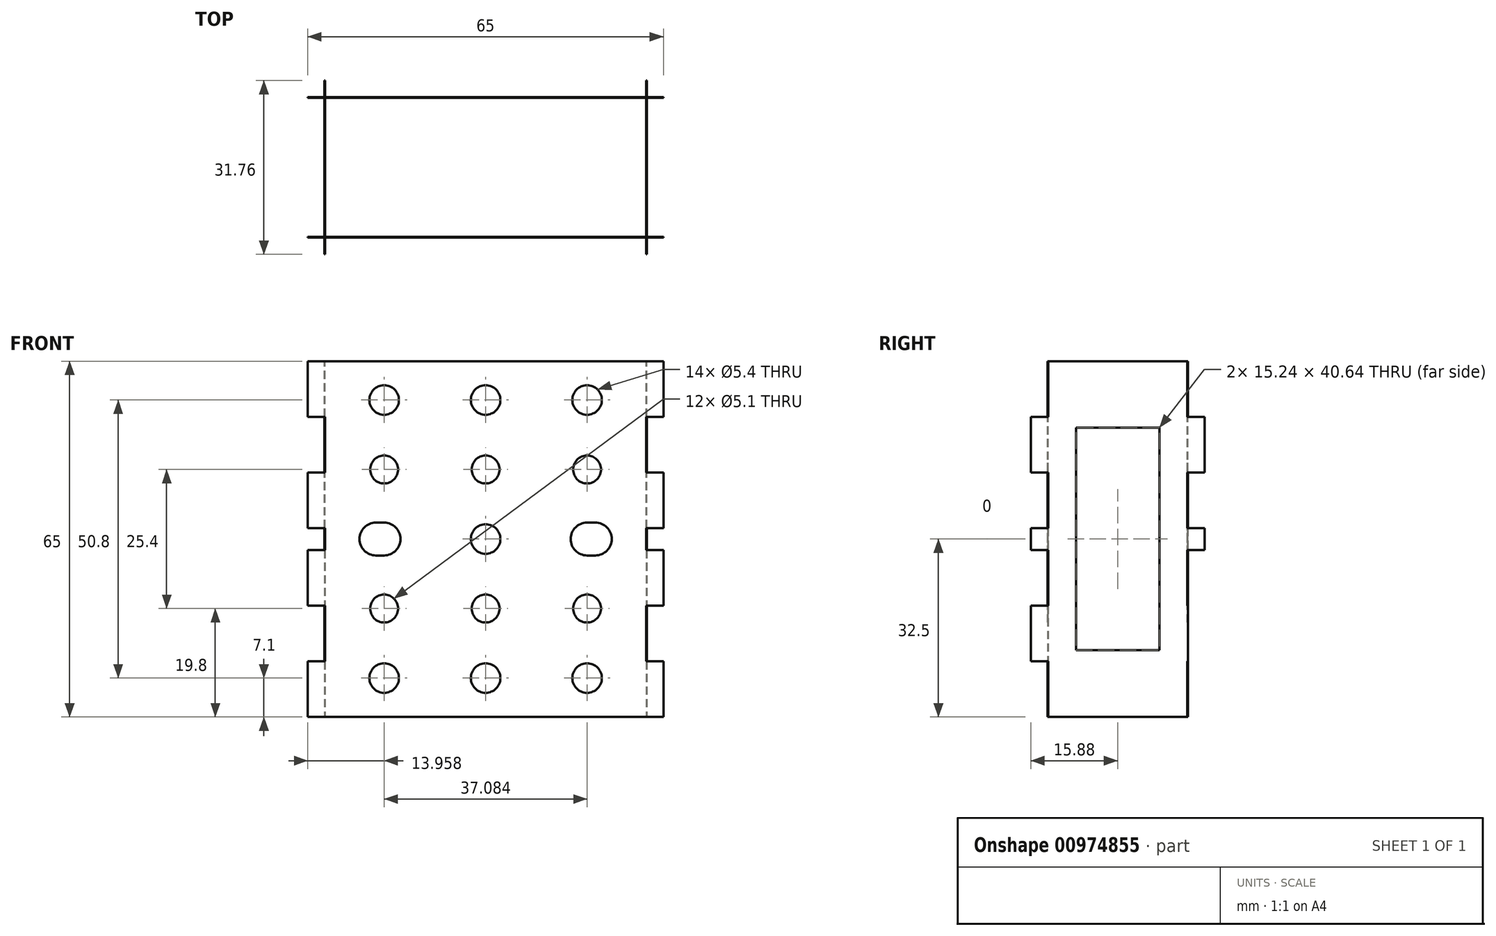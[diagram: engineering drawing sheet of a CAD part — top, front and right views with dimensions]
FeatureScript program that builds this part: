
annotation { "Feature Type Name" : "Feature", "Feature Type Description" : "" }
export const myFeature = defineFeature(function(context is Context, id is Id, definition is map)
    precondition{}
    {
        {
            assignVariable(context, id + "F0", {"name" : "thin_mdf_thickness", "anyValue" : 0.12});
        }
        {
            var Q0;
            Q0=qCreatedBy(makeId("Front.planeOp"),FACE);
            cPlane(context, id + "F1", {"entities" : qUnion([Q0]), "cplaneType" : CPlaneType.OFFSET, "offset" : 12.7 * mm, "width" : 152.4 * mm, "height" : 152.4 * mm});
        }
        {
            var Q0;
            Q0=qCreatedBy(id+"F1.planeOp",FACE);
            var sketch = newSketch(context, id + "F2", { "sketchPlane" : qUnion([Q0])});
            skLineSegment(sketch, "E0.bottom", {"start": v(32.5, 32.5) * mm, "end": v(-32.5, 32.5) * mm});
            skLineSegment(sketch, "E0.top", {"start": v(32.5, -32.5) * mm, "end": v(-32.5, -32.5) * mm});
            skLineSegment(sketch, "E0.left", {"start": v(32.5, 32.5) * mm, "end": v(32.5, 22.34) * mm});
            skLineSegment(sketch, "E0.right", {"start": v(-32.5, 32.5) * mm, "end": v(-32.5, 22.34) * mm});
            skPoint(sketch, "E0.middle", {"position": v(0, 0) * mm});
            skLineSegment(sketch, "E1", {"start": v(0, 32.5) * mm, "end": v(0, -32.5) * mm, "construction": true});
            skLineSegment(sketch, "E2", {"start": v(-32.5, 0) * mm, "end": v(32.5, 0) * mm, "construction": true});
            skLineSegment(sketch, "E3", {"start": v(0, 0) * mm, "end": v(18.54, 0) * mm, "construction": true});
            skLineSegment(sketch, "E4", {"start": v(0, 0) * mm, "end": v(0, 12.7) * mm, "construction": true});
            skLineSegment(sketch, "E5", {"start": v(0, 12.7) * mm, "end": v(0, 25.4) * mm, "construction": true});
            skCircle(sketch, "E6", {"center": v(0, 12.7) * mm, "radius": 2.55 * mm});
            skCircle(sketch, "E7", {"center": v(0, 25.4) * mm, "radius": 2.7 * mm});
            skCircle(sketch, "E8", {"center": v(0, 0) * mm, "radius": 2.7 * mm});
            skArc(sketch, "E9", {"start": v(18.54, 3) * mm, "mid": v(15.54, 0) * mm, "end": v(18.54, -3) * mm});
            skCircle(sketch, "E10.MirrorC", {"center": v(0, -12.7) * mm, "radius": 2.55 * mm});
            skCircle(sketch, "E11.MirrorC", {"center": v(0, -25.4) * mm, "radius": 2.7 * mm});
            skLineSegment(sketch, "E12", {"start": v(-32.5, -32.5) * mm, "end": v(-29.32, -32.5) * mm, "construction": true});
            skLineSegment(sketch, "E13", {"start": v(-29.33, -32.5) * mm, "end": v(-29.32, 32.5) * mm, "construction": true});
            skLineSegment(sketch, "E14", {"start": v(-32.5, -32.5) * mm, "end": v(-32.5, -22.34) * mm, "construction": true});
            skLineSegment(sketch, "E15", {"start": v(-32.5, -12.18) * mm, "end": v(-32.5, -2.02) * mm, "construction": true});
            skLineSegment(sketch, "E16", {"start": v(-32.5, -22.34) * mm, "end": v(-29.32, -22.34) * mm});
            skLineSegment(sketch, "E17", {"start": v(-32.5, -12.18) * mm, "end": v(-29.32, -12.18) * mm});
            skLineSegment(sketch, "E18", {"start": v(-29.32, -12.18) * mm, "end": v(-29.32, -22.34) * mm});
            skLineSegment(sketch, "E19", {"start": v(-32.5, -2.02) * mm, "end": v(-29.32, -2.02) * mm});
            skLineSegment(sketch, "E20", {"start": v(-29.32, -2.02) * mm, "end": v(-29.32, 0) * mm});
            skLineSegment(sketch, "E21.trimOffspring", {"start": v(-32.5, -22.34) * mm, "end": v(-32.5, -32.5) * mm});
            skLineSegment(sketch, "E22.trimOffspring", {"start": v(-32.5, -2.02) * mm, "end": v(-32.5, -12.18) * mm});
            skLineSegment(sketch, "E23.MirrorCS", {"start": v(-29.32, 12.18) * mm, "end": v(-29.32, 22.34) * mm});
            skLineSegment(sketch, "E24.MirrorCS", {"start": v(-32.5, 22.34) * mm, "end": v(-32.5, 32.5) * mm});
            skLineSegment(sketch, "E25.MirrorCS", {"start": v(-29.33, 32.5) * mm, "end": v(-29.32, -32.5) * mm, "construction": true});
            skLineSegment(sketch, "E26.MirrorCS", {"start": v(-32.5, 32.5) * mm, "end": v(-32.5, 22.34) * mm, "construction": true});
            skLineSegment(sketch, "E27.MirrorCS", {"start": v(-32.5, 22.34) * mm, "end": v(-29.32, 22.34) * mm});
            skLineSegment(sketch, "E28.MirrorCS", {"start": v(-29.32, 2.02) * mm, "end": v(-29.32, 0) * mm});
            skLineSegment(sketch, "E29.MirrorCS", {"start": v(-32.5, 2.02) * mm, "end": v(-32.5, 12.18) * mm});
            skLineSegment(sketch, "E30.MirrorCS", {"start": v(-32.5, 12.18) * mm, "end": v(-32.5, 2.02) * mm, "construction": true});
            skLineSegment(sketch, "E31.MirrorCS", {"start": v(-32.5, 2.02) * mm, "end": v(-29.32, 2.02) * mm});
            skLineSegment(sketch, "E32.MirrorCS", {"start": v(-32.5, 12.18) * mm, "end": v(-29.32, 12.18) * mm});
            skLineSegment(sketch, "E33.MirrorCS", {"start": v(29.32, 12.18) * mm, "end": v(29.32, 22.34) * mm});
            skLineSegment(sketch, "E34.MirrorCS", {"start": v(29.32, 32.5) * mm, "end": v(29.33, -32.5) * mm, "construction": true});
            skLineSegment(sketch, "E35.MirrorCS", {"start": v(29.33, 2.02) * mm, "end": v(29.33, 0) * mm});
            skLineSegment(sketch, "E36.MirrorCS", {"start": v(29.32, -12.18) * mm, "end": v(29.32, -22.34) * mm});
            skLineSegment(sketch, "E37.MirrorCS", {"start": v(29.32, -32.5) * mm, "end": v(29.32, 32.5) * mm, "construction": true});
            skLineSegment(sketch, "E38.MirrorCS", {"start": v(29.32, -2.02) * mm, "end": v(29.32, 0) * mm});
            skLineSegment(sketch, "E39.MirrorCS", {"start": v(32.5, -22.34) * mm, "end": v(32.5, -32.5) * mm});
            skLineSegment(sketch, "E40.MirrorCS", {"start": v(32.5, -2.02) * mm, "end": v(32.5, -12.18) * mm});
            skLineSegment(sketch, "E41.MirrorCS", {"start": v(32.5, 22.34) * mm, "end": v(32.5, 32.5) * mm});
            skLineSegment(sketch, "E42.MirrorCS", {"start": v(32.5, 2.02) * mm, "end": v(32.5, 12.18) * mm});
            skLineSegment(sketch, "E43.MirrorCS", {"start": v(-32.5, -32.5) * mm, "end": v(32.5, -32.5) * mm});
            skLineSegment(sketch, "E44.MirrorCS", {"start": v(32.5, 0) * mm, "end": v(-32.5, 0) * mm, "construction": true});
            skLineSegment(sketch, "E45.MirrorCS", {"start": v(32.5, -2.02) * mm, "end": v(29.32, -2.02) * mm});
            skLineSegment(sketch, "E46.MirrorCS", {"start": v(32.5, -32.5) * mm, "end": v(32.5, -22.34) * mm, "construction": true});
            skLineSegment(sketch, "E47.MirrorCS", {"start": v(32.5, -12.18) * mm, "end": v(29.32, -12.18) * mm});
            skLineSegment(sketch, "E48.MirrorCS", {"start": v(32.5, -22.34) * mm, "end": v(29.32, -22.34) * mm});
            skLineSegment(sketch, "E49.MirrorCS", {"start": v(-32.5, 32.5) * mm, "end": v(32.5, 32.5) * mm});
            skLineSegment(sketch, "E50.MirrorCS", {"start": v(32.5, 12.18) * mm, "end": v(32.5, 2.02) * mm, "construction": true});
            skLineSegment(sketch, "E51.MirrorCS", {"start": v(32.5, 2.02) * mm, "end": v(29.32, 2.02) * mm});
            skLineSegment(sketch, "E52.MirrorCS", {"start": v(32.5, 12.18) * mm, "end": v(29.32, 12.18) * mm});
            skLineSegment(sketch, "E53.MirrorCS", {"start": v(32.5, 22.34) * mm, "end": v(29.32, 22.34) * mm});
            skLineSegment(sketch, "E54.MirrorCS", {"start": v(32.5, -32.5) * mm, "end": v(29.32, -32.5) * mm, "construction": true});
            skLineSegment(sketch, "E55.MirrorCS", {"start": v(32.5, 32.5) * mm, "end": v(32.5, 22.34) * mm, "construction": true});
            skLineSegment(sketch, "E56.MirrorCS", {"start": v(32.5, -12.18) * mm, "end": v(32.5, -2.02) * mm, "construction": true});
            skLineSegment(sketch, "E57.trimOffspring", {"start": v(-32.5, 12.18) * mm, "end": v(-32.5, 0) * mm});
            skLineSegment(sketch, "E58.trimOffspring", {"start": v(32.5, 12.18) * mm, "end": v(32.5, 0) * mm});
            skLineSegment(sketch, "E59", {"start": v(-18.54, 0) * mm, "end": v(0, 0) * mm, "construction": true});
            skLineSegment(sketch, "E60", {"start": v(-9.27, 0) * mm, "end": v(-9.27, 32.5) * mm, "construction": true});
            skCircle(sketch, "E61.MirrorC", {"center": v(-18.54, 25.4) * mm, "radius": 2.7 * mm});
            skCircle(sketch, "E62.MirrorC", {"center": v(-18.54, 12.7) * mm, "radius": 2.55 * mm});
            skCircle(sketch, "E63.MirrorC", {"center": v(-18.54, -12.7) * mm, "radius": 2.55 * mm});
            skCircle(sketch, "E64.MirrorC", {"center": v(-18.54, -25.4) * mm, "radius": 2.7 * mm});
            skCircle(sketch, "E65.MirrorC", {"center": v(18.54, 25.4) * mm, "radius": 2.7 * mm});
            skCircle(sketch, "E66.MirrorC", {"center": v(18.54, 12.7) * mm, "radius": 2.55 * mm});
            skCircle(sketch, "E67.MirrorC", {"center": v(18.54, -12.7) * mm, "radius": 2.55 * mm});
            skCircle(sketch, "E68.MirrorC", {"center": v(18.54, -25.4) * mm, "radius": 2.7 * mm});
            skLineSegment(sketch, "E69", {"start": v(18.54, 0) * mm, "end": v(20.04, 0) * mm, "construction": true});
            skArc(sketch, "E70", {"start": v(20.04, -3) * mm, "mid": v(23.04, 0) * mm, "end": v(20.04, 3) * mm});
            skLineSegment(sketch, "E71", {"start": v(18.54, 0) * mm, "end": v(18.54, 3) * mm, "construction": true});
            skLineSegment(sketch, "E72", {"start": v(20.04, 0) * mm, "end": v(20.04, 3) * mm, "construction": true});
            skLineSegment(sketch, "E73", {"start": v(20.04, 0) * mm, "end": v(20.04, -3) * mm, "construction": true});
            skLineSegment(sketch, "E74", {"start": v(18.54, 0) * mm, "end": v(18.54, -3) * mm, "construction": true});
            skLineSegment(sketch, "E75", {"start": v(18.54, 3) * mm, "end": v(20.04, 3) * mm});
            skLineSegment(sketch, "E76", {"start": v(20.04, -3) * mm, "end": v(18.54, -3) * mm});
            skArc(sketch, "E77.MirrorCS", {"start": v(-20.04, -3) * mm, "mid": v(-23.04, 0) * mm, "end": v(-20.04, 3) * mm});
            skArc(sketch, "E78.MirrorCS", {"start": v(-18.54, 3) * mm, "mid": v(-15.54, 0) * mm, "end": v(-18.54, -3) * mm});
            skLineSegment(sketch, "E79.MirrorCS", {"start": v(-18.54, 3) * mm, "end": v(-20.04, 3) * mm});
            skLineSegment(sketch, "E80.MirrorCS", {"start": v(-20.04, -3) * mm, "end": v(-18.54, -3) * mm});
            skSolve(sketch);
        }
        {
            var Q0;
            Q0=makeQuery(id+"F2.imprint","IMPRINT",FACE,{"disambiguationData":[TD([[makeQuery(id+"F2.imprint","IMPRINT",EDGE,{"derivedFrom":sQuery(id+"F2.wireOp",EDGE,"E6")}),-1.0]])]});
            extrude(context, id + "F3", {"entities" : qUnion([Q0]), "depth" : (getVariable(context, 'thin_mdf_thickness')) * mm, "offsetDistance" : 25.4 * mm});
        }
        {
            var Q0;
            Q0=makeQuery(id+"F3.opExtrude","SWEPT_BODY",BODY,{"disambiguationData":[OSD([sQuery(id+"F2.wireOp",EDGE,"E0.bottom"),sQuery(id+"F2.wireOp",EDGE,"E0.top"),sQuery(id+"F2.wireOp",EDGE,"E0.left"),sQuery(id+"F2.wireOp",EDGE,"E0.right"),sQuery(id+"F2.wireOp",EDGE,"E6"),sQuery(id+"F2.wireOp",EDGE,"E7"),sQuery(id+"F2.wireOp",EDGE,"E8"),sQuery(id+"F2.wireOp",EDGE,"E9"),sQuery(id+"F2.wireOp",EDGE,"aac28c9c-199a-4393-b529-e34efc27d3f90.MirrorC"),sQuery(id+"F2.wireOp",EDGE,"E10.MirrorC"),sQuery(id+"F2.wireOp",EDGE,"E11.MirrorC")])]});
            var Q1;
            Q1=qCreatedBy(makeId("Front.planeOp"),FACE);
            mirror(context, id + "F4", {"entities" : qUnion([Q0]), "mirrorPlane" : qUnion([Q1])});
        }
        {
            var Q0;
            Q0=qCreatedBy(makeId("Front.planeOp"),FACE);
            var sketch = newSketch(context, id + "F5", { "sketchPlane" : qUnion([Q0])});
            skCircle(sketch, "E81.0", {"center": v(-18.29, 0) * mm, "radius": 2.55 * mm});
            skCircle(sketch, "E82", {"center": v(-18.29, 0) * mm, "radius": 15.88 * mm});
            skLineSegment(sketch, "E83", {"start": v(-18.29, 0) * mm, "end": v(-2.41, 0) * mm, "construction": true});
            skLineSegment(sketch, "E84", {"start": v(-2.41, 0) * mm, "end": v(0, 0) * mm, "construction": true});
            skSolve(sketch);
        }
        {
            var Q0;
            Q0=makeQuery(id+"F4.opPattern","COPY",FACE,{"derivedFrom":makeQuery(id+"F3.opExtrude","SWEPT_FACE",FACE,{"disambiguationData":[OSD([sQuery(id+"F2.wireOp",EDGE,"E18")])]}),"instanceName":"1"});
            var sketch = newSketch(context, id + "F6", { "sketchPlane" : qUnion([Q0])});
            skLineSegment(sketch, "E85", {"start": v(25.4, -32.5) * mm, "end": v(25.4, -12.18) * mm, "construction": true});
            skLineSegment(sketch, "E86.bottom", {"start": v(-7.62, -20.32) * mm, "end": v(7.62, -20.32) * mm});
            skLineSegment(sketch, "E86.top", {"start": v(-7.62, 20.32) * mm, "end": v(7.62, 20.32) * mm});
            skLineSegment(sketch, "E86.left", {"start": v(-7.62, -20.32) * mm, "end": v(-7.62, 20.32) * mm});
            skLineSegment(sketch, "E86.right", {"start": v(7.62, -20.32) * mm, "end": v(7.62, 20.32) * mm});
            skPoint(sketch, "E86.middle", {"position": v(0, 0) * mm});
            skLineSegment(sketch, "E87.0.0", {"start": v(-12.7, 12.18) * mm, "end": v(-12.7, 22.34) * mm});
            skLineSegment(sketch, "E87.0.1", {"start": v(-12.7, 22.34) * mm, "end": v(-15.88, 22.34) * mm});
            skLineSegment(sketch, "E87.0.2", {"start": v(-15.88, 22.34) * mm, "end": v(-15.88, 12.18) * mm});
            skLineSegment(sketch, "E87.0.3", {"start": v(-15.88, 12.18) * mm, "end": v(-12.7, 12.18) * mm});
            skLineSegment(sketch, "E88.0.0", {"start": v(-12.7, -2.02) * mm, "end": v(-12.7, 2.02) * mm});
            skLineSegment(sketch, "E88.0.1", {"start": v(-12.7, 2.02) * mm, "end": v(-15.88, 2.02) * mm});
            skLineSegment(sketch, "E88.0.2", {"start": v(-15.88, 2.02) * mm, "end": v(-15.88, -2.02) * mm});
            skLineSegment(sketch, "E88.0.3", {"start": v(-15.88, -2.02) * mm, "end": v(-12.7, -2.02) * mm});
            skLineSegment(sketch, "E89.0.0", {"start": v(-12.7, -22.34) * mm, "end": v(-12.7, -12.18) * mm});
            skLineSegment(sketch, "E89.0.1", {"start": v(-12.7, -12.18) * mm, "end": v(-15.88, -12.18) * mm});
            skLineSegment(sketch, "E89.0.2", {"start": v(-15.88, -12.18) * mm, "end": v(-15.88, -22.34) * mm});
            skLineSegment(sketch, "E89.0.3", {"start": v(-15.88, -22.34) * mm, "end": v(-12.7, -22.34) * mm});
            skLineSegment(sketch, "E90.0.0", {"start": v(12.7, -12.18) * mm, "end": v(12.7, -22.34) * mm});
            skLineSegment(sketch, "E90.0.1", {"start": v(12.7, -22.34) * mm, "end": v(15.88, -22.34) * mm});
            skLineSegment(sketch, "E90.0.2", {"start": v(15.88, -22.34) * mm, "end": v(15.88, -12.18) * mm});
            skLineSegment(sketch, "E90.0.3", {"start": v(15.88, -12.18) * mm, "end": v(12.7, -12.18) * mm});
            skLineSegment(sketch, "E91.0.0", {"start": v(12.7, 2.02) * mm, "end": v(12.7, -2.02) * mm});
            skLineSegment(sketch, "E91.0.1", {"start": v(12.7, -2.02) * mm, "end": v(15.88, -2.02) * mm});
            skLineSegment(sketch, "E91.0.2", {"start": v(15.88, -2.02) * mm, "end": v(15.88, 2.02) * mm});
            skLineSegment(sketch, "E91.0.3", {"start": v(15.88, 2.02) * mm, "end": v(12.7, 2.02) * mm});
            skLineSegment(sketch, "E92.0.0", {"start": v(12.7, 22.34) * mm, "end": v(12.7, 12.18) * mm});
            skLineSegment(sketch, "E92.0.1", {"start": v(12.7, 12.18) * mm, "end": v(15.88, 12.18) * mm});
            skLineSegment(sketch, "E92.0.2", {"start": v(15.88, 12.18) * mm, "end": v(15.88, 22.34) * mm});
            skLineSegment(sketch, "E92.0.3", {"start": v(15.88, 22.34) * mm, "end": v(12.7, 22.34) * mm});
            skLineSegment(sketch, "E93.0.0", {"start": v(-12.7, 2.02) * mm, "end": v(-12.7, 12.18) * mm});
            skLineSegment(sketch, "E93.0.4", {"start": v(-12.7, 22.34) * mm, "end": v(-12.7, 32.5) * mm});
            skLineSegment(sketch, "E93.0.6", {"start": v(-12.7, 32.5) * mm, "end": v(-12.7, 22.34) * mm});
            skLineSegment(sketch, "E93.0.8", {"start": v(-12.7, 22.34) * mm, "end": v(-12.7, 12.18) * mm});
            skLineSegment(sketch, "E93.0.10", {"start": v(-12.7, 12.18) * mm, "end": v(-12.7, 2.02) * mm});
            skLineSegment(sketch, "E93.0.12", {"start": v(-12.7, 2.02) * mm, "end": v(-12.7, -2.02) * mm});
            skLineSegment(sketch, "E93.0.14", {"start": v(-12.7, -2.02) * mm, "end": v(-12.7, -12.18) * mm});
            skLineSegment(sketch, "E93.0.16", {"start": v(-12.7, -12.18) * mm, "end": v(-12.7, -22.34) * mm});
            skLineSegment(sketch, "E93.0.18", {"start": v(-12.7, -22.34) * mm, "end": v(-12.7, -32.5) * mm});
            skLineSegment(sketch, "E93.0.20", {"start": v(-12.7, -32.5) * mm, "end": v(-12.7, -22.34) * mm});
            skLineSegment(sketch, "E93.0.24", {"start": v(-12.7, -12.18) * mm, "end": v(-12.7, -2.02) * mm});
            skLineSegment(sketch, "E94.0.0", {"start": v(12.7, 12.18) * mm, "end": v(12.7, 2.02) * mm});
            skLineSegment(sketch, "E94.0.4", {"start": v(12.7, -2.02) * mm, "end": v(12.7, -12.18) * mm});
            skLineSegment(sketch, "E94.0.8", {"start": v(12.7, -22.34) * mm, "end": v(12.7, -32.5) * mm});
            skLineSegment(sketch, "E94.0.10", {"start": v(12.7, -32.5) * mm, "end": v(12.7, -22.34) * mm});
            skLineSegment(sketch, "E94.0.12", {"start": v(12.7, -22.34) * mm, "end": v(12.7, -12.18) * mm});
            skLineSegment(sketch, "E94.0.14", {"start": v(12.7, -12.18) * mm, "end": v(12.7, -2.02) * mm});
            skLineSegment(sketch, "E94.0.16", {"start": v(12.7, -2.02) * mm, "end": v(12.7, 2.02) * mm});
            skLineSegment(sketch, "E94.0.18", {"start": v(12.7, 2.02) * mm, "end": v(12.7, 12.18) * mm});
            skLineSegment(sketch, "E94.0.20", {"start": v(12.7, 12.18) * mm, "end": v(12.7, 22.34) * mm});
            skLineSegment(sketch, "E94.0.22", {"start": v(12.7, 22.34) * mm, "end": v(12.7, 32.5) * mm});
            skLineSegment(sketch, "E94.0.24", {"start": v(12.7, 32.5) * mm, "end": v(12.7, 22.34) * mm});
            skLineSegment(sketch, "E95.bottom", {"start": v(-12.7, -32.5) * mm, "end": v(12.7, -32.5) * mm});
            skLineSegment(sketch, "E95.top", {"start": v(-12.7, 32.5) * mm, "end": v(12.7, 32.5) * mm});
            skSolve(sketch);
        }
        {
            var Q0;
            {var subQ1=sQuery(id+"F6.wireOp",EDGE,"vb0iRZmg-YX2T-7GjZ-xg6K-9PIDNVfWKY3m");Q0=makeQuery(id+"F6.imprint","IMPRINT",FACE,{"disambiguationData":[TD([[makeQuery(id+"F6.imprint","IMPRINT",EDGE,{"derivedFrom":subQ1}),1.0]])]});}
            var Q1;
            Q1=makeQuery(id+"F6.imprint","IMPRINT",FACE,{"disambiguationData":[TD([[makeQuery(id+"F6.imprint","IMPRINT",EDGE,{"derivedFrom":sQuery(id+"F6.wireOp",EDGE,"E87.0.0")}),1.0]])]});
            var Q2;
            Q2=makeQuery(id+"F6.imprint","IMPRINT",FACE,{"disambiguationData":[TD([[makeQuery(id+"F6.imprint","IMPRINT",EDGE,{"derivedFrom":sQuery(id+"F6.wireOp",EDGE,"E88.0.0")}),1.0]])]});
            var Q3;
            Q3=makeQuery(id+"F6.imprint","IMPRINT",FACE,{"disambiguationData":[TD([[makeQuery(id+"F6.imprint","IMPRINT",EDGE,{"derivedFrom":sQuery(id+"F6.wireOp",EDGE,"E89.0.0")}),-1.0]])]});
            var Q4;
            Q4=makeQuery(id+"F6.imprint","IMPRINT",FACE,{"disambiguationData":[TD([[makeQuery(id+"F6.imprint","IMPRINT",EDGE,{"derivedFrom":sQuery(id+"F6.wireOp",EDGE,"E90.0.0")}),1.0]])]});
            var Q5;
            Q5=makeQuery(id+"F6.imprint","IMPRINT",FACE,{"disambiguationData":[TD([[makeQuery(id+"F6.imprint","IMPRINT",EDGE,{"derivedFrom":sQuery(id+"F6.wireOp",EDGE,"E91.0.0")}),1.0]])]});
            var Q6;
            Q6=makeQuery(id+"F6.imprint","IMPRINT",FACE,{"disambiguationData":[TD([[makeQuery(id+"F6.imprint","IMPRINT",EDGE,{"derivedFrom":sQuery(id+"F6.wireOp",EDGE,"E92.0.0")}),1.0]])]});
            var Q7;
            Q7=makeQuery(id+"F6.imprint","IMPRINT",FACE,{"disambiguationData":[TD([[makeQuery(id+"F6.imprint","IMPRINT",EDGE,{"derivedFrom":sQuery(id+"F6.wireOp",EDGE,"E86.bottom")}),-1.0]])]});
            var Q8;
            Q8=makeQuery(id+"F6.imprint","IMPRINT",FACE,{"disambiguationData":[TD([[makeQuery(id+"F6.imprint","IMPRINT",EDGE,{"derivedFrom":sQuery(id+"F6.wireOp",EDGE,"E90.0.1")}),1.0]])]});
            var Q9;
            Q9=makeQuery(id+"F6.imprint","IMPRINT",FACE,{"disambiguationData":[TD([[makeQuery(id+"F6.imprint","IMPRINT",EDGE,{"derivedFrom":sQuery(id+"F6.wireOp",EDGE,"E91.0.1")}),1.0]])]});
            var Q10;
            Q10=makeQuery(id+"F6.imprint","IMPRINT",FACE,{"disambiguationData":[TD([[makeQuery(id+"F6.imprint","IMPRINT",EDGE,{"derivedFrom":sQuery(id+"F6.wireOp",EDGE,"E92.0.1")}),1.0]])]});
            var Q11;
            Q11=makeQuery(id+"F6.imprint","IMPRINT",FACE,{"disambiguationData":[TD([[makeQuery(id+"F6.imprint","IMPRINT",EDGE,{"derivedFrom":sQuery(id+"F6.wireOp",EDGE,"E88.0.1")}),1.0]])]});
            var Q12;
            Q12=makeQuery(id+"F6.imprint","IMPRINT",FACE,{"disambiguationData":[TD([[makeQuery(id+"F6.imprint","IMPRINT",EDGE,{"derivedFrom":sQuery(id+"F6.wireOp",EDGE,"E89.0.1")}),-1.0]])]});
            var Q13;
            Q13=makeQuery(id+"F6.imprint","IMPRINT",FACE,{"disambiguationData":[TD([[makeQuery(id+"F6.imprint","IMPRINT",EDGE,{"derivedFrom":sQuery(id+"F6.wireOp",EDGE,"E87.0.1")}),1.0]])]});
            extrude(context, id + "F7", {"entities" : qUnion([Q0, Q1, Q2, Q3, Q4, Q5, Q6, Q7, Q8, Q9, Q10, Q11, Q12, Q13]), "depth" : (getVariable(context, 'thin_mdf_thickness')) * mm, "offsetDistance" : 25.4 * mm});
        }
        {
            var Q0;
            Q0=makeQuery(id+"F7.opExtrude","SWEPT_BODY",BODY,{"disambiguationData":[OSD([sQuery(id+"F6.wireOp",EDGE,"ce5cbe48-56f6-4d4c-8633-94caa0cff7dd.0"),sQuery(id+"F6.wireOp",EDGE,"b131364b-ef3c-49d6-bbb2-05256cba32f9.0"),sQuery(id+"F6.wireOp",EDGE,"vb0iRZmg-YX2T-7GjZ-xg6K-9PIDNVfWKY3m"),sQuery(id+"F6.wireOp",EDGE,"HM8pEL6l-OiA3-KCzh-qviT-9IPn1mujcFzb"),sQuery(id+"F6.wireOp",EDGE,"E86.bottom"),sQuery(id+"F6.wireOp",EDGE,"E86.top"),sQuery(id+"F6.wireOp",EDGE,"E86.left"),sQuery(id+"F6.wireOp",EDGE,"E86.right"),sQuery(id+"F6.wireOp",EDGE,"E87.0.1"),sQuery(id+"F6.wireOp",EDGE,"E87.0.2"),sQuery(id+"F6.wireOp",EDGE,"E87.0.3"),sQuery(id+"F6.wireOp",EDGE,"E88.0.1"),sQuery(id+"F6.wireOp",EDGE,"E88.0.2"),sQuery(id+"F6.wireOp",EDGE,"E88.0.3"),sQuery(id+"F6.wireOp",EDGE,"E89.0.1"),sQuery(id+"F6.wireOp",EDGE,"E89.0.2"),sQuery(id+"F6.wireOp",EDGE,"E89.0.3"),sQuery(id+"F6.wireOp",EDGE,"E90.0.1"),sQuery(id+"F6.wireOp",EDGE,"E90.0.2"),sQuery(id+"F6.wireOp",EDGE,"E90.0.3"),sQuery(id+"F6.wireOp",EDGE,"E91.0.1"),sQuery(id+"F6.wireOp",EDGE,"E91.0.2"),sQuery(id+"F6.wireOp",EDGE,"E91.0.3"),sQuery(id+"F6.wireOp",EDGE,"E92.0.1"),sQuery(id+"F6.wireOp",EDGE,"E92.0.2"),sQuery(id+"F6.wireOp",EDGE,"E92.0.3")])]});
            var Q1;
            Q1=qCreatedBy(makeId("Right.planeOp"),FACE);
            mirror(context, id + "F8", {"entities" : qUnion([Q0]), "mirrorPlane" : qUnion([Q1])});
        }
    });
